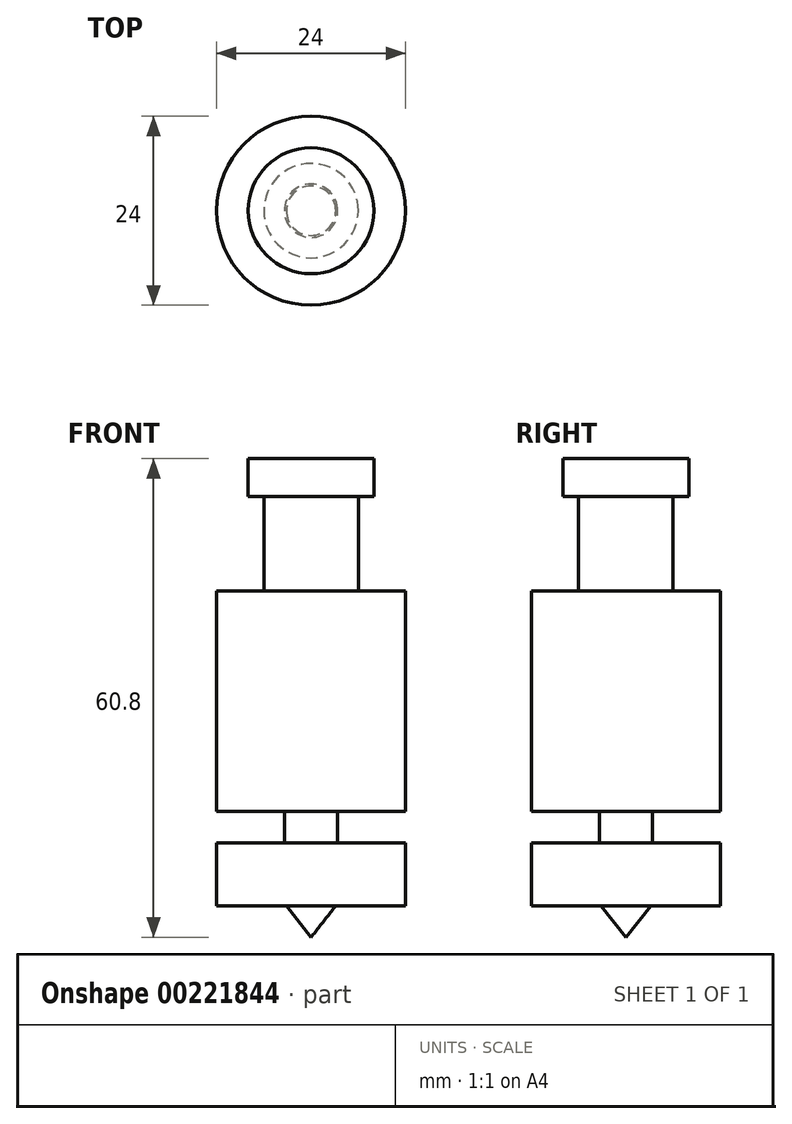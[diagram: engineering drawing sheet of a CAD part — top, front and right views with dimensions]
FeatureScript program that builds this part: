
annotation { "Feature Type Name" : "Feature", "Feature Type Description" : "" }
export const myFeature = defineFeature(function(context is Context, id is Id, definition is map)
    precondition{}
    {
        {
            var Q0;
            Q0=qCreatedBy(makeId("Front.planeOp"),FACE);
            var sketch = newSketch(context, id + "F0", { "sketchPlane" : qUnion([Q0])});
            skLineSegment(sketch, "E0", {"start": v(0, 0) * mm, "end": v(8, 0) * mm});
            skLineSegment(sketch, "E1", {"start": v(8, 0) * mm, "end": v(8, -4.8) * mm});
            skLineSegment(sketch, "E2", {"start": v(8, -4.8) * mm, "end": v(6, -4.8) * mm});
            skLineSegment(sketch, "E3", {"start": v(6, -4.8) * mm, "end": v(6, -16.8) * mm});
            skLineSegment(sketch, "E4", {"start": v(6, -16.8) * mm, "end": v(12, -16.8) * mm});
            skLineSegment(sketch, "E5", {"start": v(12, -16.8) * mm, "end": v(12, -44.8) * mm});
            skLineSegment(sketch, "E6", {"start": v(12, -56.8) * mm, "end": v(3.14, -56.8) * mm});
            skLineSegment(sketch, "E7", {"start": v(3.14, -56.8) * mm, "end": v(0, -60.8) * mm});
            skLineSegment(sketch, "E8", {"start": v(0, -60.8) * mm, "end": v(0, 0) * mm});
            skLineSegment(sketch, "E9", {"start": v(12, -48.8) * mm, "end": v(3.4, -48.8) * mm});
            skLineSegment(sketch, "E10", {"start": v(3.4, -48.8) * mm, "end": v(3.4, -44.8) * mm});
            skLineSegment(sketch, "E11", {"start": v(3.4, -44.8) * mm, "end": v(12, -44.8) * mm});
            skLineSegment(sketch, "E12.trimOffspring", {"start": v(12, -48.8) * mm, "end": v(12, -56.8) * mm});
            skSolve(sketch);
        }
        {
            var Q0;
            Q0 = qSketchRegion(id + "F0", true);
            var Q1;
            Q1=sQuery(id+"F0.wireOp",EDGE,"E8");
            revolve(context, id + "F1", {"entities" : qUnion([Q0]), "axis" : qUnion([Q1]), "revolveType" : RevolveType.FULL});
        }
    });
